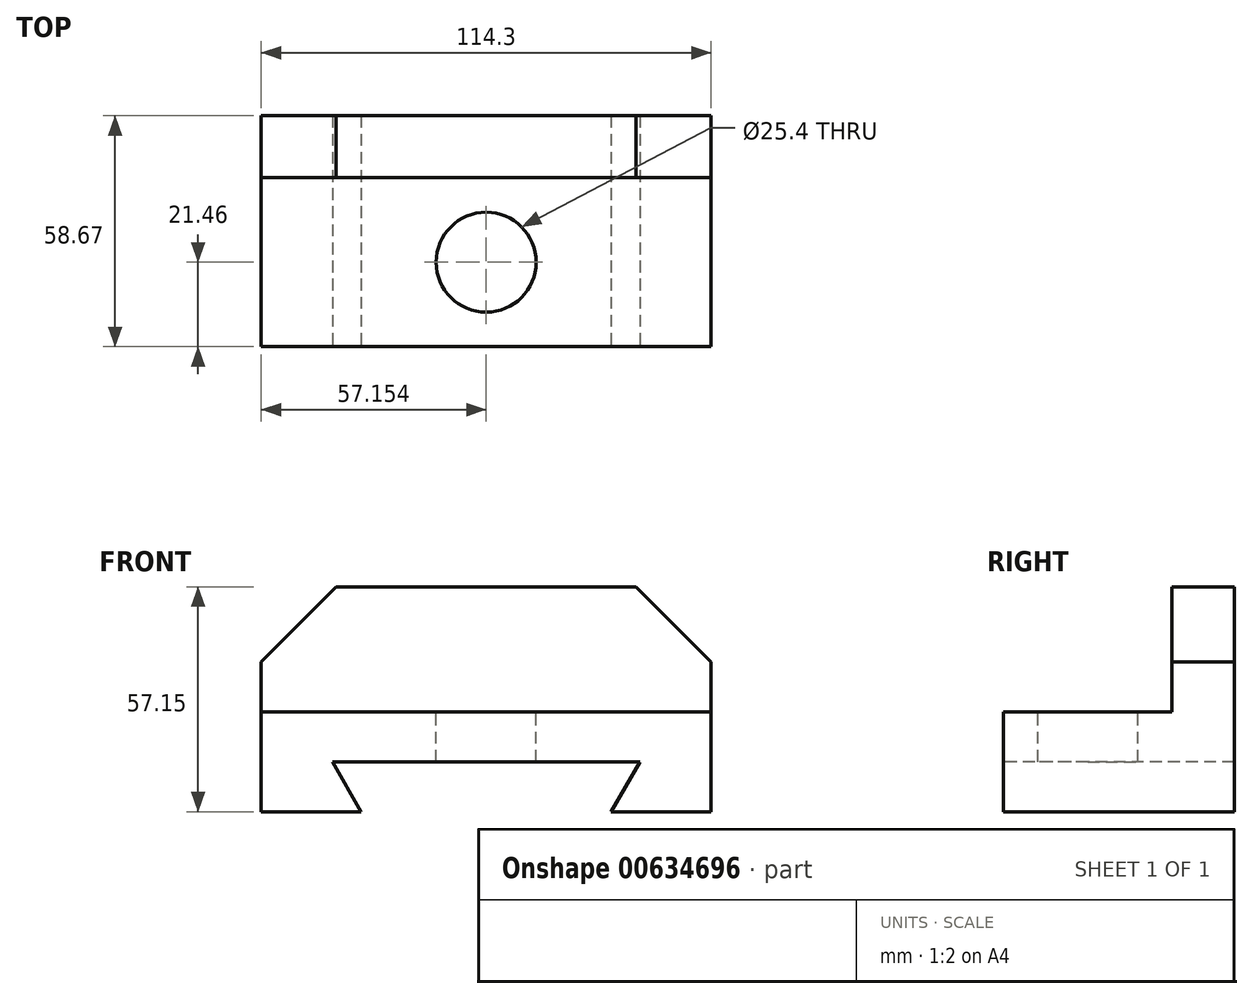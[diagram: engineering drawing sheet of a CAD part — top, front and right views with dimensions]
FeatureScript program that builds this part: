
annotation { "Feature Type Name" : "Feature", "Feature Type Description" : "" }
export const myFeature = defineFeature(function(context is Context, id is Id, definition is map)
    precondition{}
    {
        {
            var Q0;
            Q0=qCreatedBy(makeId("Top.planeOp"),FACE);
            var sketch = newSketch(context, id + "F0", { "sketchPlane" : qUnion([Q0])});
            skLineSegment(sketch, "E0.bottom", {"start": v(-49.17, -33.24) * mm, "end": v(65.13, -33.24) * mm});
            skLineSegment(sketch, "E0.top", {"start": v(-49.17, 25.43) * mm, "end": v(65.13, 25.43) * mm});
            skLineSegment(sketch, "E0.left", {"start": v(-49.17, -33.24) * mm, "end": v(-49.17, 25.43) * mm});
            skLineSegment(sketch, "E0.right", {"start": v(65.13, -33.24) * mm, "end": v(65.13, 25.43) * mm});
            skSolve(sketch);
        }
        {
            var Q0;
            Q0=makeQuery(id+"F0.imprint","IMPRINT",FACE,{"disambiguationData":[TD([[makeQuery(id+"F0.imprint","IMPRINT",EDGE,{"derivedFrom":sQuery(id+"F0.wireOp",EDGE,"E0.bottom")}),1.0]])]});
            extrude(context, id + "F1", {"entities" : qUnion([Q0]), "depth" : 57.15 * mm, "offsetDistance" : 25.4 * mm});
        }
        {
            var Q0;
            Q0=makeQuery(id+"F1.opExtrude","SWEPT_FACE",FACE,{"disambiguationData":[OSD([sQuery(id+"F0.wireOp",EDGE,"E0.right")])]});
            var sketch = newSketch(context, id + "F2", { "sketchPlane" : qUnion([Q0])});
            skLineSegment(sketch, "E1.bottom", {"start": v(-33.24, 25.4) * mm, "end": v(9.68, 25.4) * mm});
            skLineSegment(sketch, "E1.top", {"start": v(-33.24, 57.15) * mm, "end": v(9.68, 57.15) * mm});
            skLineSegment(sketch, "E1.left", {"start": v(-33.24, 25.4) * mm, "end": v(-33.24, 57.15) * mm});
            skLineSegment(sketch, "E1.right", {"start": v(9.68, 25.4) * mm, "end": v(9.68, 57.15) * mm});
            skSolve(sketch);
        }
        {
            var Q0;
            Q0 = qSketchRegion(id + "F2", true);
            extrude(context, id + "F3", {"entities" : qUnion([Q0]), "operationType" : NewBodyOperationType.REMOVE, "oppositeDirection" : true, "depth" : 143.26 * mm, "offsetDistance" : 25.4 * mm});
        }
        {
            var Q0;
            Q0=makeQuery(id+"F3.boolean.opBoolean","COPY",FACE,{"derivedFrom":makeQuery(id+"F3.opExtrude","SWEPT_FACE",FACE,{"disambiguationData":[OSD([sQuery(id+"F2.wireOp",EDGE,"E1.right")])]})});
            var sketch = newSketch(context, id + "F4", { "sketchPlane" : qUnion([Q0])});
            skLineSegment(sketch, "E2", {"start": v(65.13, 57.15) * mm, "end": v(46.08, 57.15) * mm});
            skLineSegment(sketch, "E3", {"start": v(65.13, 57.15) * mm, "end": v(65.13, 38.1) * mm});
            skLineSegment(sketch, "E4", {"start": v(46.08, 57.15) * mm, "end": v(65.13, 38.1) * mm});
            skLineSegment(sketch, "E5.MirrorCS", {"start": v(-49.17, 57.15) * mm, "end": v(-30.12, 57.15) * mm});
            skLineSegment(sketch, "E6.MirrorCS", {"start": v(-30.12, 57.15) * mm, "end": v(-49.17, 38.1) * mm});
            skLineSegment(sketch, "E7.MirrorCS", {"start": v(-49.17, 57.15) * mm, "end": v(-49.17, 38.1) * mm});
            skSolve(sketch);
        }
        {
            var Q0;
            Q0=makeQuery(id+"F4.imprint","IMPRINT",FACE,{"disambiguationData":[TD([[makeQuery(id+"F4.imprint","IMPRINT",EDGE,{"derivedFrom":sQuery(id+"F4.wireOp",EDGE,"E2")}),-1.0]])]});
            var Q1;
            Q1=makeQuery(id+"F4.imprint","IMPRINT",FACE,{"disambiguationData":[TD([[makeQuery(id+"F4.imprint","IMPRINT",EDGE,{"derivedFrom":sQuery(id+"F4.wireOp",EDGE,"E5.MirrorCS")}),-1.0]])]});
            extrude(context, id + "F5", {"entities" : qUnion([Q0, Q1]), "operationType" : NewBodyOperationType.REMOVE, "oppositeDirection" : true, "depth" : 25.4 * mm, "offsetDistance" : 25.4 * mm});
        }
        {
            var Q0;
            Q0=makeQuery(id+"F1.opExtrude","SWEPT_FACE",FACE,{"disambiguationData":[OSD([sQuery(id+"F0.wireOp",EDGE,"E0.bottom")])]});
            var sketch = newSketch(context, id + "F6", { "sketchPlane" : qUnion([Q0])});
            skLineSegment(sketch, "E8.bottom", {"start": v(-23.77, 12.7) * mm, "end": v(39.73, 12.7) * mm});
            skLineSegment(sketch, "E8.top", {"start": v(-23.77, 0) * mm, "end": v(39.73, 0) * mm});
            skLineSegment(sketch, "E9", {"start": v(-23.77, 0) * mm, "end": v(-31.1, 12.7) * mm});
            skLineSegment(sketch, "E10", {"start": v(-23.77, 12.7) * mm, "end": v(-31.1, 12.7) * mm});
            skLineSegment(sketch, "E11", {"start": v(39.73, 0) * mm, "end": v(47.07, 12.7) * mm});
            skLineSegment(sketch, "E12", {"start": v(39.73, 12.7) * mm, "end": v(47.07, 12.7) * mm});
            skSolve(sketch);
        }
        {
            var Q0;
            Q0=makeQuery(id+"F6.imprint","IMPRINT",FACE,{"disambiguationData":[TD([[makeQuery(id+"F6.imprint","IMPRINT",EDGE,{"derivedFrom":sQuery(id+"F6.wireOp",EDGE,"E8.bottom")}),-1.0]])]});
            extrude(context, id + "F7", {"entities" : qUnion([Q0]), "operationType" : NewBodyOperationType.REMOVE, "oppositeDirection" : true, "depth" : 101.1 * mm, "offsetDistance" : 25.4 * mm});
        }
        {
            var Q0;
            Q0=makeQuery(id+"F3.boolean.opBoolean","COPY",FACE,{"derivedFrom":makeQuery(id+"F3.opExtrude","SWEPT_FACE",FACE,{"disambiguationData":[OSD([sQuery(id+"F2.wireOp",EDGE,"E1.bottom")])]})});
            var sketch = newSketch(context, id + "F8", { "sketchPlane" : qUnion([Q0])});
            skCircle(sketch, "E13", {"center": v(7.98, -11.78) * mm, "radius": 12.7 * mm});
            skSolve(sketch);
        }
        {
            var Q0;
            Q0 = qSketchRegion(id + "F8", true);
            extrude(context, id + "F9", {"entities" : qUnion([Q0]), "operationType" : NewBodyOperationType.REMOVE, "oppositeDirection" : true, "depth" : 25.4 * mm, "offsetDistance" : 25.4 * mm});
        }
    });
